# Revit family: Keilhauer-Swish-Lounge_Chair+
name_source: partatom
category: Furniture
units: mm (PartAtom-declared; Revit-internal decimal feet)

## family parameters
Always vertical = Yes
Cut with Voids When Loaded = No
OmniClass Number = 23.40.20.00
OmniClass Title = General Furniture and Specialties
Room Calculation Point = No
Shared = No
Work Plane-Based = No

## types (3) — shared parameters
Assembly Code = E2020200
Default Elevation = 0"
Depth = 29"
Height = 33"
Keynote = 12500
Low Emitting Finish = Yes
Low Emitting Material = Yes
Manufacturer = Keilhauer
Product Documentation Link = https://keilhauer.com
Revit File Built By = https://servex-us.com
Salvage or Reuse = Yes
Type Comments = Swish
URL = https://keilhauer.com
Width = 30 1/2"
zero-valued in all types: Percentage of Recycled Content

## per-type parameters (varying)
| type | Casters | Description | Glides | Swivel |
| 99000 | No | Lounge chair with Glides | Yes | No |
| 99020 | Yes | Lounge chair with Casters | No | No |
| 99010 | No | Lounge chair with Swivel | No | Yes |

note: column(s) folded — value = type name in every type: Model

## geometry (parser evidence)
native form markers: Sweep x5
no freeform markers — native parametric forms only
